# Revit family: NBS_HeatraeSadia_StrgWtrHtrsElctrc_Multipoint10and15
name_source: partatom
category: Plumbing Fixtures
revit_build: Autodesk Revit 2014 (Build: 20130709_2115(x64)
units: mm (PartAtom-declared; Revit-internal decimal feet)

## types (4) — shared parameters
Accessories = Accessory pack U1 (95:970:352), Accessory pack U2 (95:970:351), Accessory pack U3 (95:970:354), Accessory pack U7 (95:970:360)
Arrangement = Multipoint – mains supply
AssetType = Fixed
CW Connection = Yes
CasingFinish = White stove enamel
Color = White
Connections = Heater: 15 mm copper tube tails; Tundish: Inlet - 1/2" BSP male, outlet - 3/4" BSP female; Service valve: 15 mm compression
Controls = For use with standard tap or mixer
Depth = 252 mm  [stored 0.826772 ft]
Description = Unvented point of use storage water heater
DurationUnit = year
Features = Element ‘on’ indicator, no anodes to inspect or replace, suitable for use with any standard tap or mixer, suitable replacement for cistern-type water heaters where improved water flow is required.
Fixing = Floor or wall fixed
FlowRate = To suit draw off requirements
HW Connection = Yes
HeatTransferSurfaceArea = 0
IPCode = IPX4
IfcExportAs = IfcBoilerType
IfcExportType = WATER
IsWaterStorageHeater = Yes
ManufacturerName = Heatrae Sadia
ManufacturerURL = www.heatraesadia.com
Material = Outer casing: Plastic top moulding with steel base and centre section; Water container: Replaceable heavy gauge copper; Heat unit: Replaceable rod-type element sheathed in corrosion resistant alloy
NBSCertification = http://www.nationalbimlibrary.com
NBSDescription = Storage water heaters, electric
NBSReference = 90-15-35/440
NominalLength = 267 mm  [stored 0.875984 ft]
NominalWidth = 252 mm  [stored 0.826772 ft]
OutletTemperatureRange = 10, 70
PartialLoadEfficiencyCurves = 0
PressureRating = 0
ProductInformation = www.heatraesadia.com/docs/POU_unvented_water_heating_brochure.pdf
SafetyFeatures = Temperature and pressure relief valve set to open at 7 bar or 90°C, resettable over temperature cut-out
StorageWaterHeaterMaterial = NBS_Concept
ThermalInsulation = CFC/HCFC free (ODP zero) flame-retardant expanded polyurethane
ThirdPartyCertification = Kiwa approved
Uniclass2 = 90-90-46/428
Uniclass2015Description = Electric storage water heaters
Uniclass2015Reference = Pr_60_60_96_28
Uniclass2015Version = Products v1.1
Vent Connection = No
Version = 1
WarrantyDurationParts = 5
WarrantyDurationUnit = year
WarrantyStartDate = 1900-12-31T23:59:59
Waste Connection = No
WaterInletTemperatureRange = 0
Width = 267 mm  [stored 0.875984 ft]
zero-valued in all types: HeatOutput, NominalEfficiency, NominalEnergyConsumption, NominalPartLoadRatio

## per-type parameters (varying)
| type | BIMObjectName | BodyHeight | Height | ModelNumber | ModelReference | Name | NominalHeight | Rating | Size | WaterStorageCapacity | Weight |
| 10-3kW | NBS_HeatraeSadia_StorageWaterHeatersElectric_Multipoint10-3kW | 529 mm | 572 mm | 95:050:143 | Multipoint 10 3kW | StorageWaterHeatersElectric_Multipoint10-3kW_HeatraeSadia | 572 mm | 3.0 kW | 572 x 267 x 252 mm | 10 | 16.9 |
| 10-4.5kW | NBS_HeatraeSadia_StorageWaterHeatersElectric_Multipoint10-4.5kW | 529 mm | 572 mm | 95:050:145 | Multipoint 10 4.5kW | StorageWaterHeatersElectric_Multipoint10-4.5kW_HeatraeSadia | 572 mm | 4.5 kW | 572 x 267 x 252 mm | 10 | 16.9 |
| 15-3kW | NBS_HeatraeSadia_StorageWaterHeatersElectric_Multipoint15-3kW | 685 mm | 728 mm  [stored 2.38845 ft] | 95:050:144 | Multipoint 15 3kW | StorageWaterHeatersElectric_Multipoint15-3kW_HeatraeSadia | 728 mm  [stored 2.38845 ft] | 3.0 kW | 728 x 267 x 252 mm | 15 | 23.8 |
| 15-4.5kW | NBS_HeatraeSadia_StorageWaterHeatersElectric_Multipoint15-4.5kW | 685 mm | 728 mm  [stored 2.38845 ft] | 95:050:146 | Multipoint 15 4.5kW | StorageWaterHeatersElectric_Multipoint15-4.5kW_HeatraeSadia | 728 mm  [stored 2.38845 ft] | 4.5 kW | 728 x 267 x 252 mm | 15 | 23.8 |

note: [stored X ft] marks values corroborated as IEEE doubles in the binary element streams (Revit-internal decimal feet)

## geometry (parser evidence)
native form markers: Blend x13, Sweep x1
no freeform markers — native parametric forms only
